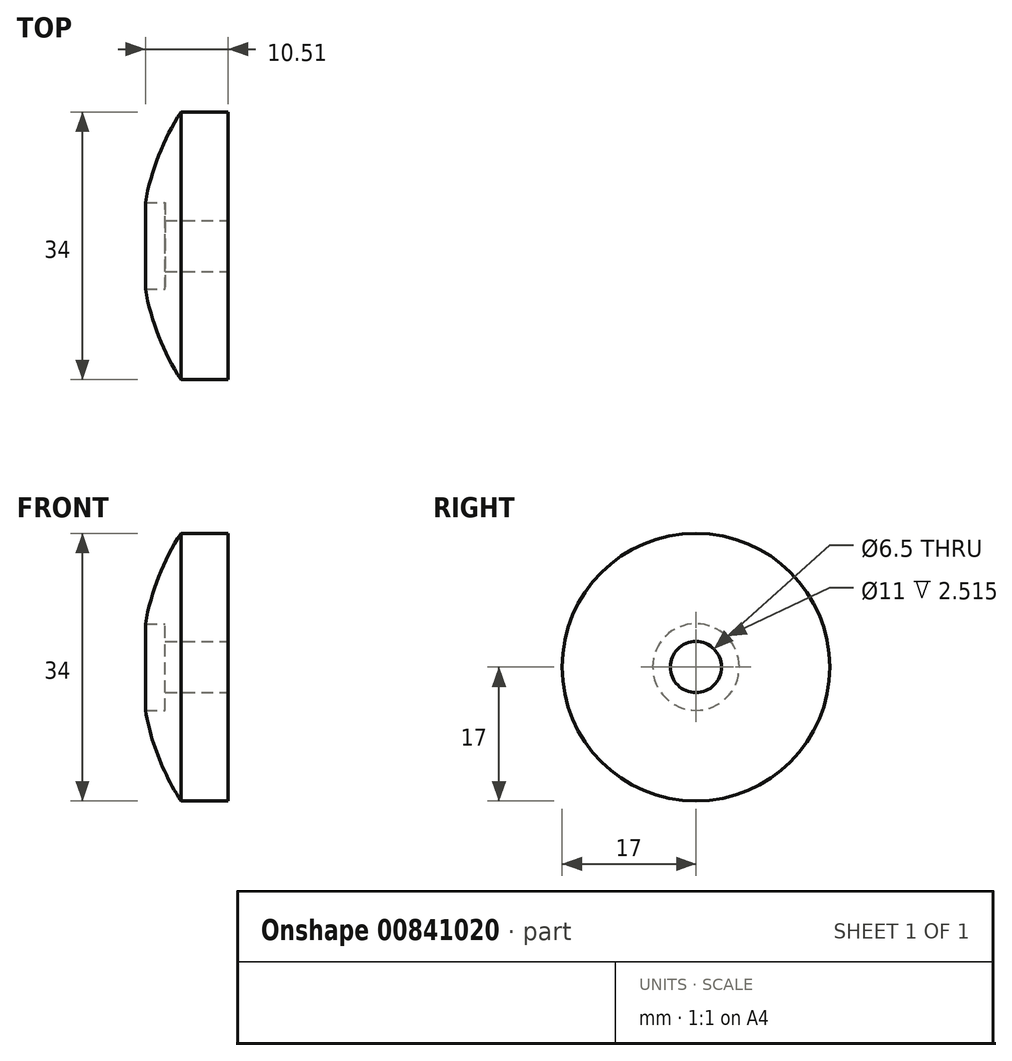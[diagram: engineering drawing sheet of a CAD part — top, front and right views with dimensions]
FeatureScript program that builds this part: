
annotation { "Feature Type Name" : "Feature", "Feature Type Description" : "" }
export const myFeature = defineFeature(function(context is Context, id is Id, definition is map)
    precondition{}
    {
        {
            var Q0;
            Q0=qCreatedBy(makeId("Front.planeOp"),FACE);
            var sketch = newSketch(context, id + "F0", { "sketchPlane" : qUnion([Q0])});
            skLineSegment(sketch, "E0.bottom", {"start": v(0, 0) * mm, "end": v(-11, 0) * mm, "construction": true});
            skLineSegment(sketch, "E0.top", {"start": v(0, 17) * mm, "end": v(-6, 17) * mm});
            skLineSegment(sketch, "E0.left", {"start": v(0, 0) * mm, "end": v(0, 17) * mm});
            skArc(sketch, "E1", {"start": v(-6, 17) * mm, "mid": v(-8.83, 11.47) * mm, "end": v(-10.51, 5.5) * mm});
            skLineSegment(sketch, "E2", {"start": v(-11, 0) * mm, "end": v(-11, 19.88) * mm, "construction": true});
            skLineSegment(sketch, "E3", {"start": v(-10.51, 5.5) * mm, "end": v(-8, 5.5) * mm});
            skLineSegment(sketch, "E4", {"start": v(-8, 5.5) * mm, "end": v(-8, 3.25) * mm});
            skLineSegment(sketch, "E5", {"start": v(-8, 3.25) * mm, "end": v(0, 3.25) * mm});
            skSolve(sketch);
        }
        {
            var Q0;
            {var subQ2=sQuery(id+"F0.wireOp",EDGE,"E0.top");Q0=makeQuery(id+"F0.imprint","IMPRINT",FACE,{"disambiguationData":[TD([[makeQuery(id+"F0.imprint","IMPRINT",EDGE,{"derivedFrom":subQ2}),1.0]])]});}
            var Q1;
            Q1=sQuery(id+"F0.wireOp",EDGE,"E0.bottom");
            revolve(context, id + "F1", {"surfaceOperationType" : NewSurfaceOperationType.NEW, "entities" : qUnion([Q0]), "axis" : qUnion([Q1]), "revolveType" : RevolveType.FULL});
        }
    });
